FCSTD DOCUMENT  (FreeCAD 0.18.4R)
Label: 3-bedr_1fl_130720
License: All rights reserved
LicenseURL: http://en.wikipedia.org/wiki/All_rights_reserved
objects: Part::Part2DObjectPython×132, Part::Feature×3, Sketcher::SketchObject×2, Part::FeaturePython×2, App::DocumentObjectGroup×2
note: 139 computed .brp shape members not serialized (recipe doc carries the construction recipe); baked Part::Feature solids carry a one-line shape summary decoded from their .brp

FEATURE [Part::Part2DObjectPython] Rectangle1621  label="кровать_2сп_001"  # Draft 2D object (typed FeaturePython)
  ChamferSize = 0
  Columns = 1
  FilletRadius = 0
  Height = 1600
  Length = 2100
  MakeFace = false
  Placement = pos=(1550,11900,0) rot=(0,0,1;1.5708rad)
  Rows = 1
FEATURE [Part::Part2DObjectPython] Rectangle1622  label="тумба_001"  # Draft 2D object (typed FeaturePython)
  ChamferSize = 0
  Columns = 1
  FilletRadius = 0
  Height = 400
  Length = 400
  MakeFace = false
  Placement = pos=(-150,13600,0) rot=(0,0,1;1.5708rad)
  Rows = 1
FEATURE [Part::Part2DObjectPython] Rectangle1623  label="тумба_010"  # Draft 2D object (typed FeaturePython)
  ChamferSize = 0
  Columns = 1
  FilletRadius = 0
  Height = 400
  Length = 400
  MakeFace = false
  Placement = pos=(2050,13600,0) rot=(0,0,1;1.5708rad)
  Rows = 1
FEATURE [Part::Part2DObjectPython] Rectangle1624  # Draft 2D object (typed FeaturePython)
  ChamferSize = 0
  Columns = 1
  FilletRadius = 0
  Height = 600
  Length = 600
  MakeFace = false
  Placement = pos=(2950,13400,0) rot=(0,0,1;1.5708rad)
  Rows = 1
FEATURE [Part::Part2DObjectPython] Rectangle1625  # Draft 2D object (typed FeaturePython)
  ChamferSize = 0
  Columns = 1
  FilletRadius = 0
  Height = 600
  Length = 600
  MakeFace = false
  Placement = pos=(2950,12800,0) rot=(0,0,1;1.5708rad)
  Rows = 1
FEATURE [Part::Part2DObjectPython] Rectangle1626  # Draft 2D object (typed FeaturePython)
  ChamferSize = 0
  Columns = 1
  FilletRadius = 0
  Height = 600
  Length = 600
  MakeFace = false
  Placement = pos=(2950,12200,0) rot=(0,0,1;1.5708rad)
  Rows = 1
FEATURE [Part::Part2DObjectPython] Rectangle1628  # Draft 2D object (typed FeaturePython)
  ChamferSize = 0
  Columns = 1
  FilletRadius = 0
  Height = 3100
  Length = 3900
  MakeFace = false
  Placement = pos=(3200,10900,0) rot=(0,0,1;0rad)
  Rows = 1
FEATURE [Part::Part2DObjectPython] Wire351  # Draft 2D object (typed FeaturePython)
  ChamferSize = 0
  Closed = false
  End = (2950,12200,0)
  FilletRadius = 0
  Length = 5691.17
  MakeFace = false
  Placement = pos=(2350,12200,0) rot=(0,0,1;1.5708rad)
  Points = (8) [(0,0,0),(600,-600,0),(1200,0,0),(1800,-600,0),(1800,0,0),(1200,-600,0),(600,0,0),(0,-600,0)]
  Start = (2350,12200,0)
  Subdivisions = 0
FEATURE [Part::Part2DObjectPython] Rectangle1629  # Draft 2D object (typed FeaturePython)
  ChamferSize = 0
  Columns = 1
  FilletRadius = 0
  Height = 600
  Length = 600
  MakeFace = false
  Placement = pos=(3800,12200,0) rot=(0,0,1;1.5708rad)
  Rows = 1
FEATURE [Part::Part2DObjectPython] Rectangle1630  # Draft 2D object (typed FeaturePython)
  ChamferSize = 0
  Columns = 1
  FilletRadius = 0
  Height = 600
  Length = 600
  MakeFace = false
  Placement = pos=(3800,12800,0) rot=(0,0,1;1.5708rad)
  Rows = 1
FEATURE [Part::Part2DObjectPython] Rectangle1631  # Draft 2D object (typed FeaturePython)
  ChamferSize = 0
  Columns = 1
  FilletRadius = 0
  Height = 600
  Length = 600
  MakeFace = false
  Placement = pos=(3800,13400,0) rot=(0,0,1;1.5708rad)
  Rows = 1
FEATURE [Part::Part2DObjectPython] Wire352  # Draft 2D object (typed FeaturePython)
  ChamferSize = 0
  Closed = false
  End = (3800,12200,0)
  FilletRadius = 0
  Length = 5691.17
  MakeFace = false
  Placement = pos=(3200,12200,0) rot=(0,0,1;1.5708rad)
  Points = (8) [(0,0,0),(600,-600,0),(1200,0,0),(1800,-600,0),(1800,0,0),(1200,-600,0),(600,0,0),(0,-600,0)]
  Start = (3200,12200,0)
  Subdivisions = 0
FEATURE [Part::Part2DObjectPython] Rectangle1632  label="тумба_011"  # Draft 2D object (typed FeaturePython)
  ChamferSize = 0
  Columns = 1
  FilletRadius = 0
  Height = 400
  Length = 400
  MakeFace = false
  Placement = pos=(4500,13600,0) rot=(0,0,1;1.5708rad)
  Rows = 1
FEATURE [Part::Part2DObjectPython] Rectangle1633  label="кровать_2сп_002"  # Draft 2D object (typed FeaturePython)
  ChamferSize = 0
  Columns = 1
  FilletRadius = 0
  Height = 1600
  Length = 2100
  MakeFace = false
  Placement = pos=(6200,11900,0) rot=(0,0,1;1.5708rad)
  Rows = 1
FEATURE [Part::Part2DObjectPython] Rectangle1634  label="тумба_012"  # Draft 2D object (typed FeaturePython)
  ChamferSize = 0
  Columns = 1
  FilletRadius = 0
  Height = 400
  Length = 400
  MakeFace = false
  Placement = pos=(6700,13600,0) rot=(0,0,1;1.5708rad)
  Rows = 1
FEATURE [Part::Part2DObjectPython] Rectangle1635  label="Д-90_013"  # Draft 2D object (typed FeaturePython)
  ChamferSize = 0
  Columns = 1
  FilletRadius = 0
  Height = 900
  Length = 100
  MakeFace = true
  Placement = pos=(4250,10800,0) rot=(0,0,1;1.5708rad)
  Rows = 1
FEATURE [Part::Part2DObjectPython] Rectangle1636  label="Д-90_012"  # Draft 2D object (typed FeaturePython)
  ChamferSize = 0
  Columns = 1
  FilletRadius = 0
  Height = 900
  Length = 100
  MakeFace = true
  Placement = pos=(2800,10800,0) rot=(0,0,1;1.5708rad)
  Rows = 1
FEATURE [Part::Part2DObjectPython] Rectangle1639  # Draft 2D object (typed FeaturePython)
  ChamferSize = 0
  Columns = 1
  FilletRadius = 0
  Height = 1800
  Length = 2600
  MakeFace = false
  Placement = pos=(-900,9000,0) rot=(0,0,1;0rad)
  Rows = 1
FEATURE [Part::Part2DObjectPython] Rectangle1640  # Draft 2D object (typed FeaturePython)
  ChamferSize = 0
  Columns = 1
  FilletRadius = 0
  Height = 600
  Length = 600
  MakeFace = false
  Placement = pos=(1800,8300,0) rot=(0,0,1;1.5708rad)
  Rows = 1
FEATURE [Part::Part2DObjectPython] Rectangle1641  # Draft 2D object (typed FeaturePython)
  ChamferSize = 0
  Columns = 1
  FilletRadius = 0
  Height = 600
  Length = 600
  MakeFace = false
  Placement = pos=(1200,8300,0) rot=(0,0,1;1.5708rad)
  Rows = 1
FEATURE [Part::Part2DObjectPython] Rectangle1643  # Draft 2D object (typed FeaturePython)
  ChamferSize = 0
  Columns = 1
  FilletRadius = 0
  Height = 600
  Length = 600
  MakeFace = false
  Placement = pos=(300,8300,0) rot=(0,0,1;1.5708rad)
  Rows = 1
FEATURE [Part::Part2DObjectPython] Rectangle1644  # Draft 2D object (typed FeaturePython)
  ChamferSize = 0
  Columns = 1
  FilletRadius = 0
  Height = 600
  Length = 600
  MakeFace = false
  Placement = pos=(-300,8300,0) rot=(0,0,1;1.5708rad)
  Rows = 1
FEATURE [Part::Part2DObjectPython] Rectangle1645  # Draft 2D object (typed FeaturePython)
  ChamferSize = 0
  Columns = 1
  FilletRadius = 0
  Height = 1800
  Length = 1400
  MakeFace = false
  Placement = pos=(-900,7100,0) rot=(0,0,1;0rad)
  Rows = 1
FEATURE [Part::Part2DObjectPython] Rectangle1659  label="Д-90_009"  # Draft 2D object (typed FeaturePython)
  ChamferSize = 0
  Columns = 1
  FilletRadius = 0
  Height = 100
  Length = 900
  MakeFace = true
  Placement = pos=(600,7250,0) rot=(0,0,1;1.5708rad)
  Rows = 1
FEATURE [Part::Part2DObjectPython] Rectangle1660  label="Д-90_011"  # Draft 2D object (typed FeaturePython)
  ChamferSize = 0
  Columns = 1
  FilletRadius = 0
  Height = 100
  Length = 900
  MakeFace = true
  Placement = pos=(4500,9750,0) rot=(0,0,1;1.5708rad)
  Rows = 1
FEATURE [Part::Part2DObjectPython] Rectangle1663  label="Д-90_007"  # Draft 2D object (typed FeaturePython)
  ChamferSize = 0
  Columns = 1
  FilletRadius = 0
  Height = 400
  Length = 900
  MakeFace = true
  Placement = pos=(-900,7250,0) rot=(0,0,1;1.5708rad)
  Rows = 1
FEATURE [Part::Part2DObjectPython] Rectangle1665  # Draft 2D object (typed FeaturePython)
  ChamferSize = 0
  Columns = 1
  FilletRadius = 0
  Height = 3000
  Length = 2600
  MakeFace = false
  Placement = pos=(4500,7800,0) rot=(0,0,1;0rad)
  Rows = 1
FEATURE [Part::Part2DObjectPython] Rectangle1666  # Draft 2D object (typed FeaturePython)
  ChamferSize = 0
  Columns = 1
  FilletRadius = 0
  Height = 1800
  Length = 1200
  MakeFace = false
  Placement = pos=(3200,7700,0) rot=(0,0,1;0rad)
  Rows = 1
FEATURE [Part::Part2DObjectPython] Rectangle1668  # Draft 2D object (typed FeaturePython)
  ChamferSize = 0
  Columns = 1
  FilletRadius = 0
  Height = 600
  Length = 400
  MakeFace = false
  Placement = pos=(3600,8900,0) rot=(0,0,1;0rad)
  Rows = 1
FEATURE [Part::Part2DObjectPython] Circle042  # Draft 2D object (typed FeaturePython)
  FirstAngle = 0
  LastAngle = 0
  MakeFace = false
  Placement = pos=(3800,9100,0) rot=(0,0,1;0rad)
  Radius = 100
FEATURE [Part::Part2DObjectPython] Rectangle1671  label="Д-90_010"  # Draft 2D object (typed FeaturePython)
  ChamferSize = 0
  Columns = 1
  FilletRadius = 0
  Height = 100
  Length = 900
  MakeFace = true
  Placement = pos=(1800,9750,0) rot=(0,0,1;1.5708rad)
  Rows = 1
FEATURE [Part::Part2DObjectPython] Rectangle1672  # Draft 2D object (typed FeaturePython)
  ChamferSize = 0
  Columns = 1
  FilletRadius = 0
  Height = 400
  Length = 600
  MakeFace = false
  Placement = pos=(4400,7700,0) rot=(0,0,1;1.5708rad)
  Rows = 1
FEATURE [Part::Feature] Ellipse027
  Placement = pos=(4200,8000,0) rot=(0,0,1;1.5708rad)
  shape: bbox 200 x 400 x 2e-07 mm, 0 faces, 0 solids (baked)
FEATURE [Part::Part2DObjectPython] Rectangle1673  # Draft 2D object (typed FeaturePython)
  ChamferSize = 0
  Columns = 1
  FilletRadius = 0
  Height = 800
  Length = 1800
  MakeFace = false
  Placement = pos=(-100,9000,0) rot=(0,0,1;1.5708rad)
  Rows = 1
FEATURE [Part::Feature] Ellipse028
  Placement = pos=(-500,9900,0) rot=(0,0,1;1.5708rad)
  shape: bbox 600 x 1400 x 2e-07 mm, 0 faces, 0 solids (baked)
FEATURE [Part::Part2DObjectPython] Rectangle1674  # Draft 2D object (typed FeaturePython)
  ChamferSize = 0
  Columns = 1
  FilletRadius = 0
  Height = 400
  Length = 600
  MakeFace = false
  Placement = pos=(1400,9000,0) rot=(0,0,1;1.5708rad)
  Rows = 1
FEATURE [Part::Part2DObjectPython] Circle043  # Draft 2D object (typed FeaturePython)
  FirstAngle = 0
  LastAngle = 0
  MakeFace = false
  Placement = pos=(1200,9400,0) rot=(0,0,1;1.5708rad)
  Radius = 100
FEATURE [Part::Part2DObjectPython] Rectangle1675  # Draft 2D object (typed FeaturePython)
  ChamferSize = 0
  Columns = 1
  FilletRadius = 0
  Height = 600
  Length = 400
  MakeFace = false
  Placement = pos=(700,9000,0) rot=(0,0,1;1.5708rad)
  Rows = 1
FEATURE [Part::Feature] Ellipse029
  Placement = pos=(400,9200,0) rot=(0,0,1;3.14159rad)
  shape: bbox 400 x 200 x 2e-07 mm, 0 faces, 0 solids (baked)
FEATURE [Part::Part2DObjectPython] Rectangle1676  label="кровать_1.5сп_001"  # Draft 2D object (typed FeaturePython)
  ChamferSize = 0
  Columns = 1
  FilletRadius = 0
  Height = 1200
  Length = 2100
  MakeFace = false
  Placement = pos=(4500,7800,0) rot=(0,0,1;0rad)
  Rows = 1
FEATURE [Sketcher::SketchObject] Sketch214  label="стол угловой002"
  Placement = pos=(7100,10800,0) rot=(0,0,1;3.14159rad)
  sketch-geometry (9):
    g0: LineSegment StartX=1400 StartY=0 StartZ=0 EndX=0 EndY=0 EndZ=0
    g1: LineSegment StartX=0 StartY=0 StartZ=0 EndX=0 EndY=1300 EndZ=0
    g2: LineSegment StartX=0 StartY=1300 StartZ=0 EndX=370 EndY=1300 EndZ=0
    g3: LineSegment StartX=470 StartY=1200 StartZ=0 EndX=470 EndY=900 EndZ=0
    g4: LineSegment StartX=1400 StartY=0 StartZ=0 EndX=1400 EndY=500 EndZ=0
    g5: LineSegment StartX=1300 StartY=600 StartZ=0 EndX=770 EndY=600 EndZ=0
    g6: ArcOfCircle CenterX=770 CenterY=900 CenterZ=0 NormalX=0 NormalY=0 NormalZ=1 AngleXU=0 Radius=300 StartAngle=3.14159 EndAngle=4.71239
    g7: ArcOfCircle CenterX=1300 CenterY=500 CenterZ=0 NormalX=0 NormalY=0 NormalZ=1 AngleXU=0 Radius=100 StartAngle=1e-16 EndAngle=1.5708
    g8: ArcOfCircle CenterX=370 CenterY=1200 CenterZ=0 NormalX=0 NormalY=0 NormalZ=1 AngleXU=0 Radius=100 StartAngle=5e-16 EndAngle=1.5708
  constraints (25):
    c: Horizontal(g0)
    c: Coincident(g0,g1)
    c: Vertical(g1)
    c: Coincident(g1,g2)
    c: Horizontal(g2)
    c: Coincident(g0,g4)
    c: Horizontal(g5)
    c: Coincident(g6,g3)
    c: Coincident(g6,g5)
    c: Parallel(g3,g1)
    c: Distance(g1) = 1300
    c: Distance(g0) = 1400
    c: Vertical(g4)
    c: Coincident(g0,g-1)
    c: Radius(g6) = 300
    c: DistanceY(g5,g6) = 300
    c: DistanceY(g6,g3) = 0
    c: Tangent(g5,g7) = -1.5708
    c: Tangent(g4,g7) = -1.5708
    c: Radius(g7) = 100
    c: DistanceY(g0,g5) = 600
    c: Tangent(g2,g8) = 1.5708
    c: Tangent(g3,g8) = 1.5708
    c: Radius(g8) = 100
    c: DistanceX(g1,g3) = 470
FEATURE [Sketcher::SketchObject] Sketch215  label="кресло 45'002"
  Placement = pos=(6347.49,9947.49,0) rot=(0,0,1;2.35619rad)
  sketch-geometry (11):
    g0: LineSegment StartX=-280 StartY=-350 StartZ=0 EndX=280 EndY=-350 EndZ=0
    g1: LineSegment StartX=330 StartY=-300 StartZ=0 EndX=330 EndY=300 EndZ=0
    g2: LineSegment StartX=280 StartY=350 StartZ=0 EndX=-280 EndY=350 EndZ=0
    g3: LineSegment StartX=-330 StartY=300 StartZ=0 EndX=-330 EndY=-300 EndZ=0
    g4: ArcOfCircle CenterX=-280 CenterY=300 CenterZ=0 NormalX=0 NormalY=0 NormalZ=1 AngleXU=0 Radius=50 StartAngle=1.5708 EndAngle=3.14159
    g5: ArcOfCircle CenterX=280 CenterY=300 CenterZ=0 NormalX=0 NormalY=0 NormalZ=1 AngleXU=0 Radius=50 StartAngle=-9e-16 EndAngle=1.5708
    g6: ArcOfCircle CenterX=280 CenterY=-300 CenterZ=0 NormalX=0 NormalY=0 NormalZ=1 AngleXU=0 Radius=50 StartAngle=4.71239 EndAngle=6.28319
    g7: ArcOfCircle CenterX=-280 CenterY=-300 CenterZ=0 NormalX=0 NormalY=0 NormalZ=1 AngleXU=0 Radius=50 StartAngle=3.14159 EndAngle=4.71239
    g8: LineSegment StartX=-330 StartY=200 StartZ=0 EndX=330 EndY=200 EndZ=0
    g9: LineSegment StartX=-230 StartY=200 StartZ=0 EndX=-230 EndY=-350 EndZ=0
    g10: LineSegment StartX=230 StartY=200 StartZ=0 EndX=230 EndY=-350 EndZ=0
  constraints (29):
    c: Horizontal(g0)
    c: Vertical(g1)
    c: Vertical(g3)
    c: Tangent(g2,g4) = -1.5708
    c: Tangent(g3,g4) = -1.5708
    c: Tangent(g2,g5) = -1.5708
    c: Tangent(g1,g5) = -1.5708
    c: Tangent(g0,g6) = -1.5708
    c: Tangent(g1,g6) = -1.5708
    c: Tangent(g3,g7) = -1.5708
    c: Tangent(g0,g7) = -1.5708
    c: DistanceY(g0,g2) = 700
    c: DistanceX(g3,g1) = 660
    c: Equal(g4,g5)
    c: Equal(g7,g6)
    c: Radius(g5) = 50
    c: Symmetric(g2,g2,g-2)
    c: Symmetric(g2,g0,g-1)
    c: PointOnObject(g8,g3)
    c: PointOnObject(g8,g1)
    c: Horizontal(g8)
    c: DistanceY(g8,g2) = 150
    c: PointOnObject(g9,g8)
    c: PointOnObject(g9,g0)
    c: Vertical(g9)
    c: PointOnObject(g10,g0)
    c: Vertical(g10)
    c: DistanceX(g10,g8) = 100
    c: Symmetric(g10,g9,g-2)
FEATURE [Part::Part2DObjectPython] Rectangle1677  label="шкаф_002"  # Draft 2D object (typed FeaturePython)
  ChamferSize = 0
  Columns = 1
  FilletRadius = 0
  Height = 1500
  Length = 450
  MakeFace = false
  Placement = pos=(6650,7800,0) rot=(0,0,1;0rad)
  Rows = 1
FEATURE [Part::Part2DObjectPython] Rectangle1680  # Draft 2D object (typed FeaturePython)
  ChamferSize = 0
  Columns = 1
  FilletRadius = 0
  Height = 1000
  Length = 3850
  MakeFace = false
  Placement = pos=(-900,6000,0) rot=(0,0,1;0rad)
  Rows = 1
FEATURE [Part::Part2DObjectPython] Rectangle1683  # Draft 2D object (typed FeaturePython)
  ChamferSize = 0
  Columns = 1
  FilletRadius = 0
  Height = 3275
  Length = 250
  MakeFace = false
  Placement = pos=(2950,3525,0) rot=(0,0,1;0rad)
  Rows = 1
FEATURE [Part::Part2DObjectPython] Wire356  # Draft 2D object (typed FeaturePython)
  ChamferSize = 0
  Closed = true
  End = (1800,8900,0)
  FilletRadius = 0
  Length = 4594.11
  MakeFace = false
  Placement = pos=(1800,8300,0) rot=(0,0,1;1.5708rad)
  Points = (6) [(0,600,0),(600,1200,0),(0,1200,0),(600,600,0),(0,-2.27374e-13,0),(600,0,0)]
  Start = (1200,8300,0)
  Subdivisions = 0
FEATURE [Part::Part2DObjectPython] Circle044  # Draft 2D object (typed FeaturePython)
  FirstAngle = 0
  LastAngle = 0
  MakeFace = false
  Placement = pos=(-10100,-3800,0) rot=(0,0,1;1.5708rad)
  Radius = 75
FEATURE [Part::FeaturePython] Array001  # Draft array (typed FeaturePython)
  Angle = 360
  ArrayType = 0
  Axis = (0,0,1)
  Base = -> Circle044
  Center = (0,0,0)
  Fuse = false
  IntervalAxis = (0,0,0)
  IntervalX = (250,0,0)
  IntervalY = (0,250,0)
  IntervalZ = (0,0,1)
  NumberPolar = 1
  NumberX = 2
  NumberY = 2
  NumberZ = 1
  Placement = pos=(11200,-500,0) rot=(0,0,1;1.5708rad)
FEATURE [Part::Part2DObjectPython] ShapeString051  label="надпись 052"  # Draft 2D object (typed FeaturePython)
  FontFile = <path>
  Placement = pos=(4718.84,6023.87,0) rot=(0,0,1;0rad)
  Size = 200
  String = Х
  Tracking = 0
FEATURE [Part::Part2DObjectPython] ShapeString052  label="надпись 053"  # Draft 2D object (typed FeaturePython)
  FontFile = <path>
  Placement = pos=(5211.98,3398.06,0) rot=(0,0,1;0rad)
  Size = 200
  String = ПМ
  Tracking = 0
FEATURE [Part::Part2DObjectPython] Rectangle1685  # Draft 2D object (typed FeaturePython)
  ChamferSize = 0
  Columns = 1
  FilletRadius = 0
  Height = 600
  Length = 600
  MakeFace = false
  Placement = pos=(7100,7100,0) rot=(0,0,1;1.5708rad)
  Rows = 1
FEATURE [Part::Part2DObjectPython] ShapeString053  label="надпись 054"  # Draft 2D object (typed FeaturePython)
  FontFile = <path>
  Placement = pos=(5959.55,7315.43,0) rot=(0,0,1;0rad)
  Size = 200
  String = СшМ
  Tracking = 0
FEATURE [Part::Part2DObjectPython] Rectangle1686  # Draft 2D object (typed FeaturePython)
  ChamferSize = 0
  Columns = 1
  FilletRadius = 0
  Height = 600
  Length = 600
  MakeFace = false
  Placement = pos=(6500,7100,0) rot=(0,0,1;1.5708rad)
  Rows = 1
FEATURE [Part::Part2DObjectPython] ShapeString054  label="надпись 055"  # Draft 2D object (typed FeaturePython)
  FontFile = <path>
  Placement = pos=(6622.1,7310.04,0) rot=(0,0,1;0rad)
  Size = 200
  String = СМ
  Tracking = 0
FEATURE [Part::Part2DObjectPython] Rectangle1687  # Draft 2D object (typed FeaturePython)
  ChamferSize = 0
  Columns = 1
  FilletRadius = 0
  Height = 400
  Length = 500
  MakeFace = false
  Placement = pos=(4950.18,7090.81,0) rot=(0,0,1;1.5708rad)
  Rows = 1
FEATURE [Part::Part2DObjectPython] ShapeString055  label="надпись 056"  # Draft 2D object (typed FeaturePython)
  FontFile = <path>
  Placement = pos=(4580.51,7258.99,0) rot=(0,0,1;0rad)
  Size = 200
  String = Кт
  Tracking = 0
FEATURE [Part::Part2DObjectPython] Rectangle1690  # Draft 2D object (typed FeaturePython)
  ChamferSize = 0
  Columns = 1
  FilletRadius = 0
  Height = 900
  Length = 900
  MakeFace = false
  Placement = pos=(900,3200,0) rot=(0,0,1;1.5708rad)
  Rows = 1
FEATURE [Part::Part2DObjectPython] Rectangle1692  # Draft 2D object (typed FeaturePython)
  ChamferSize = 0
  Columns = 1
  FilletRadius = 0
  Height = 1500
  Length = 100
  MakeFace = false
  Placement = pos=(1150,6800,0) rot=(0,0,1;1.5708rad)
  Rows = 1
FEATURE [Part::Part2DObjectPython] Rectangle1693  # Draft 2D object (typed FeaturePython)
  ChamferSize = 0
  Columns = 1
  FilletRadius = 0
  Height = 900
  Length = 900
  MakeFace = false
  Placement = pos=(1800,3200,0) rot=(0,0,1;1.5708rad)
  Rows = 1
FEATURE [Part::Part2DObjectPython] Rectangle1699  # Draft 2D object (typed FeaturePython)
  ChamferSize = 0
  Columns = 1
  FilletRadius = 0
  Height = 300
  Length = 450
  MakeFace = false
  Placement = pos=(3700,4600,0) rot=(0,0,1;1.5708rad)
  Rows = 1
FEATURE [Part::Part2DObjectPython] Rectangle1700  # Draft 2D object (typed FeaturePython)
  ChamferSize = 0
  Columns = 1
  FilletRadius = 0
  Height = 300
  Length = 450
  MakeFace = false
  Placement = pos=(3700,5200,0) rot=(0,0,1;1.5708rad)
  Rows = 1
FEATURE [Part::Part2DObjectPython] Rectangle1701  # Draft 2D object (typed FeaturePython)
  ChamferSize = 0
  Columns = 1
  FilletRadius = 0
  Height = 750
  Length = 1400
  MakeFace = false
  Placement = pos=(3400,4400,0) rot=(0,0,1;1.5708rad)
  Rows = 1
FEATURE [Part::Part2DObjectPython] Rectangle1702  # Draft 2D object (typed FeaturePython)
  ChamferSize = 0
  Columns = 1
  FilletRadius = 0
  Height = 900
  Length = 900
  MakeFace = false
  Placement = pos=(9.095e-13,3200,0) rot=(0,0,1;1.5708rad)
  Rows = 1
FEATURE [Part::Part2DObjectPython] Rectangle1705  # Draft 2D object (typed FeaturePython)
  ChamferSize = 0
  Columns = 1
  FilletRadius = 0
  Height = 11600
  Length = 8800
  MakeFace = false
  Placement = pos=(-1300,2800,0) rot=(0,0,1;0rad)
  Rows = 1
FEATURE [Part::Part2DObjectPython] Rectangle1706  # Draft 2D object (typed FeaturePython)
  ChamferSize = 0
  Columns = 1
  FilletRadius = 0
  Height = 750
  Length = 600
  MakeFace = false
  Placement = pos=(4500,5700,0) rot=(0,0,1;0rad)
  Rows = 1
FEATURE [Part::Part2DObjectPython] ShapeString056  label="надпись 057"  # Draft 2D object (typed FeaturePython)
  FontFile = <path>
  Placement = pos=(4707.38,3404.17,0) rot=(0,0,1;0rad)
  Size = 200
  String = Х
  Tracking = 0
FEATURE [Part::Part2DObjectPython] ShapeString057  label="надпись 058"  # Draft 2D object (typed FeaturePython)
  FontFile = <path>
  Placement = pos=(-678.733,7585.68,0) rot=(0,0,1;0rad)
  Size = 200
  String = 2.5 м2
  Tracking = 0
FEATURE [Part::Part2DObjectPython] ShapeString058  label="надпись 059"  # Draft 2D object (typed FeaturePython)
  FontFile = <path>
  Placement = pos=(94.7917,4343.06,0) rot=(0,0,1;0rad)
  Size = 200
  String = общая: 86.4 м2
  Tracking = 0
FEATURE [Part::Part2DObjectPython] ShapeString059  label="надпись 060"  # Draft 2D object (typed FeaturePython)
  FontFile = <path>
  Placement = pos=(5103.91,4383.33,0) rot=(0,0,1;0rad)
  Size = 200
  String = 6.5 м2
  Tracking = 0
FEATURE [Part::Part2DObjectPython] ShapeString060  label="надпись 061"  # Draft 2D object (typed FeaturePython)
  FontFile = <path>
  Placement = pos=(5045.75,9315.62,0) rot=(0,0,1;0rad)
  Size = 200
  String = 7,8 м2
  Tracking = 0
FEATURE [Part::Part2DObjectPython] ShapeString061  label="надпись 062"  # Draft 2D object (typed FeaturePython)
  FontFile = <path>
  Placement = pos=(3342.88,8524.74,0) rot=(0,0,1;0rad)
  Size = 200
  String = 2.2 м2
  Tracking = 0
FEATURE [Part::Part2DObjectPython] ShapeString062  label="надпись 063"  # Draft 2D object (typed FeaturePython)
  FontFile = <path>
  Placement = pos=(4725.26,11395.7,0) rot=(0,0,1;0rad)
  Size = 200
  String = 12 м2
  Tracking = 0
FEATURE [Part::Part2DObjectPython] ShapeString063  label="надпись 064"  # Draft 2D object (typed FeaturePython)
  FontFile = <path>
  Placement = pos=(1676.22,7683.33,0) rot=(0,0,1;0rad)
  Size = 200
  String = 8.5 м2
  Tracking = 0
FEATURE [Part::Part2DObjectPython] ShapeString064  label="надпись 065"  # Draft 2D object (typed FeaturePython)
  FontFile = <path>
  Placement = pos=(79.2535,9812.37,0) rot=(0,0,1;0rad)
  Size = 200
  String = 4,7 м2
  Tracking = 0
FEATURE [Part::Part2DObjectPython] ShapeString065  label="надпись 066"  # Draft 2D object (typed FeaturePython)
  FontFile = <path>
  Placement = pos=(228.385,11411.1,0) rot=(0,0,1;0rad)
  Size = 200
  String = 11,9 м2
  Tracking = 0
FEATURE [Part::Part2DObjectPython] ShapeString066  label="надпись 067"  # Draft 2D object (typed FeaturePython)
  FontFile = <path>
  Placement = pos=(5451.04,6700,0) rot=(0,0,1;0rad)
  Size = 200
  String = 5.2 м2
  Tracking = 0
FEATURE [Part::Part2DObjectPython] Rectangle1707  label="ОК-120_001"  # Draft 2D object (typed FeaturePython)
  ChamferSize = 0
  Columns = 1
  FilletRadius = 0
  Height = 400
  Length = 1200
  MakeFace = true
  Placement = pos=(-900,11600,0) rot=(0,0,1;1.5708rad)
  Rows = 1
FEATURE [Part::Part2DObjectPython] Rectangle1708  label="ОК-120_007"  # Draft 2D object (typed FeaturePython)
  ChamferSize = 0
  Columns = 1
  FilletRadius = 0
  Height = 400
  Length = 1200
  MakeFace = true
  Placement = pos=(7500,11600,0) rot=(0,0,1;1.5708rad)
  Rows = 1
FEATURE [Part::Part2DObjectPython] Rectangle1716  label="OK-90_001"  # Draft 2D object (typed FeaturePython)
  ChamferSize = 0
  Columns = 1
  FilletRadius = 0
  Height = 400
  Length = 900
  MakeFace = true
  Placement = pos=(-900,9400,0) rot=(0,0,1;1.5708rad)
  Rows = 1
FEATURE [Part::Part2DObjectPython] ShapeString067  label="надпись 068"  # Draft 2D object (typed FeaturePython)
  FontFile = <path>
  Placement = pos=(667.361,4991.49,0) rot=(0,0,1;0rad)
  Size = 200
  String = 19.5 м2
  Tracking = 0
FEATURE [Part::Part2DObjectPython] Rectangle1717  # Draft 2D object (typed FeaturePython)
  ChamferSize = 0
  Columns = 1
  FilletRadius = 0
  Height = 9800
  Length = 15000
  MakeFace = false
  Placement = pos=(8000,-100,0) rot=(0,0,1;1.5708rad)
  Rows = 1
FEATURE [Part::Part2DObjectPython] Line1006  # Draft 2D object (typed FeaturePython)
  ChamferSize = 0
  Closed = false
  End = (3100,14900,0)
  FilletRadius = 0
  Length = 15000
  MakeFace = false
  Placement = pos=(-3800,-7900,0) rot=(0,0,1;1.5708rad)
  Points = (2) [(7800,-6900,0),(22800,-6900,0)]
  Start = (3100,-100,0)
  Subdivisions = 0
FEATURE [Part::Part2DObjectPython] Rectangle  # Draft 2D object (typed FeaturePython)
  ChamferSize = 0
  Columns = 1
  FilletRadius = 0
  Height = 3100
  Length = 3850
  MakeFace = false
  Placement = pos=(-900,10900,0) rot=(0,0,1;0rad)
  Rows = 1
FEATURE [Part::Part2DObjectPython] Wire  # Draft 2D object (typed FeaturePython)
  ChamferSize = 0
  Closed = false
  End = (-900,8300,0)
  FilletRadius = 0
  Length = 3994.11
  MakeFace = true
  Placement = pos=(-900,8900,0) rot=(0,0,1;0rad)
  Points = (6) [(0,0,0),(600,-600,0),(1200,-1.81899e-12,0),(1200,-600,0),(600,-1.81899e-12,0),(-1.13687e-13,-600,0)]
  Start = (-900,8900,0)
  Subdivisions = 0
FEATURE [Part::Part2DObjectPython] Rectangle1719  # Draft 2D object (typed FeaturePython)
  ChamferSize = 0
  Columns = 1
  FilletRadius = 0
  Height = 2000
  Length = 2600
  MakeFace = false
  Placement = pos=(4500,5700,0) rot=(0,0,1;0rad)
  Rows = 1
FEATURE [Part::Part2DObjectPython] Wire358  # Draft 2D object (typed FeaturePython)
  ChamferSize = 0
  Closed = true
  End = (1800,8900,0)
  FilletRadius = 0
  Length = 38150
  MakeFace = false
  Placement = pos=(1800,10800,0) rot=(0,0,1;0rad)
  Points = (23) [(0,0,0),(2600,0,0),(2600,-1200,0),(1150,-1200,0),(1150,-4000,0),(1150,-4000,0),(2600,-4000,0),(2600,-5200,0),(5300,-5200,0),(5300,-7600,0),+13 more]
  Start = (1800,10800,0)
  Subdivisions = 0
FEATURE [Part::Part2DObjectPython] Rectangle1725  label="OK-90_007"  # Draft 2D object (typed FeaturePython)
  ChamferSize = 0
  Columns = 1
  FilletRadius = 0
  Height = 400
  Length = 900
  MakeFace = true
  Placement = pos=(7500,9400,0) rot=(0,0,1;1.5708rad)
  Rows = 1
FEATURE [Part::Part2DObjectPython] Rectangle1726  label="Д-90_001"  # Draft 2D object (typed FeaturePython)
  ChamferSize = 0
  Columns = 1
  FilletRadius = 0
  Height = 400
  Length = 900
  MakeFace = true
  Placement = pos=(7500,6100,0) rot=(0,0,1;1.5708rad)
  Rows = 1
FEATURE [Part::Part2DObjectPython] Rectangle1727  # Draft 2D object (typed FeaturePython)
  ChamferSize = 0
  Columns = 1
  FilletRadius = 0
  Height = 600
  Length = 300
  MakeFace = false
  Placement = pos=(7100,5300,0) rot=(0,0,1;1.5708rad)
  Rows = 1
FEATURE [Part::Part2DObjectPython] Rectangle1728  # Draft 2D object (typed FeaturePython)
  ChamferSize = 0
  Columns = 1
  FilletRadius = 0
  Height = 600
  Length = 600
  MakeFace = false
  Placement = pos=(7100,4700,0) rot=(0,0,1;1.5708rad)
  Rows = 1
FEATURE [Part::Part2DObjectPython] Rectangle1729  # Draft 2D object (typed FeaturePython)
  ChamferSize = 0
  Columns = 1
  FilletRadius = 0
  Height = 600
  Length = 900
  MakeFace = false
  Placement = pos=(7100,3800,0) rot=(0,0,1;1.5708rad)
  Rows = 1
FEATURE [Part::Part2DObjectPython] Rectangle1732  label="Д-90_008"  # Draft 2D object (typed FeaturePython)
  ChamferSize = 0
  Columns = 1
  FilletRadius = 0
  Height = 400
  Length = 900
  MakeFace = true
  Placement = pos=(3375,2800,0) rot=(0,0,1;0rad)
  Rows = 1
FEATURE [Part::Part2DObjectPython] Rectangle1733  label="OK-90_008"  # Draft 2D object (typed FeaturePython)
  ChamferSize = 0
  Columns = 1
  FilletRadius = 0
  Height = 400
  Length = 900
  MakeFace = true
  Placement = pos=(1850,2800,0) rot=(0,0,1;0rad)
  Rows = 1
FEATURE [Part::Part2DObjectPython] Rectangle1734  label="Д-70_001"  # Draft 2D object (typed FeaturePython)
  ChamferSize = 0
  Columns = 1
  FilletRadius = 0
  Height = 700
  Length = 100
  MakeFace = true
  Placement = pos=(5950,5600,0) rot=(0,0,1;1.5708rad)
  Rows = 1
FEATURE [Part::Part2DObjectPython] Rectangle1735  label="Д-70_002"  # Draft 2D object (typed FeaturePython)
  ChamferSize = 0
  Columns = 1
  FilletRadius = 0
  Height = 250
  Length = 700
  MakeFace = true
  Placement = pos=(3200,7800,0) rot=(0,0,1;1.5708rad)
  Rows = 1
FEATURE [Part::Part2DObjectPython] Rectangle1736  label="шкаф_001"  # Draft 2D object (typed FeaturePython)
  ChamferSize = 0
  Columns = 1
  FilletRadius = 0
  Height = 450
  Length = 2600
  MakeFace = false
  Placement = pos=(-900,6550,0) rot=(0,0,1;0rad)
  Rows = 1
FEATURE [Part::Part2DObjectPython] Rectangle1738  label="ОК-120_010"  # Draft 2D object (typed FeaturePython)
  ChamferSize = 0
  Columns = 1
  FilletRadius = 0
  Height = 400
  Length = 1200
  MakeFace = true
  Placement = pos=(5300,2800,0) rot=(0,0,1;0rad)
  Rows = 1
FEATURE [Part::Part2DObjectPython] Rectangle1739  label="ОК-120_009"  # Draft 2D object (typed FeaturePython)
  ChamferSize = 0
  Columns = 1
  FilletRadius = 0
  Height = 400
  Length = 1200
  MakeFace = true
  Placement = pos=(-300,2800,0) rot=(0,0,1;0rad)
  Rows = 1
FEATURE [Part::Part2DObjectPython] Rectangle1740  label="ОК-120_008"  # Draft 2D object (typed FeaturePython)
  ChamferSize = 0
  Columns = 1
  FilletRadius = 0
  Height = 400
  Length = 1200
  MakeFace = true
  Placement = pos=(-900,4400,0) rot=(0,0,1;1.5708rad)
  Rows = 1
FEATURE [Part::Part2DObjectPython] Rectangle1741  label="Rectangle1739"  # Draft 2D object (typed FeaturePython)
  ChamferSize = 0
  Columns = 1
  FilletRadius = 0
  Height = 600
  Length = 600
  MakeFace = false
  Placement = pos=(6500,3200,0) rot=(0,0,1;0rad)
  Rows = 1
FEATURE [Part::Part2DObjectPython] Rectangle1742  label="Rectangle1740"  # Draft 2D object (typed FeaturePython)
  ChamferSize = 0
  Columns = 1
  FilletRadius = 0
  Height = 900
  Length = 600
  MakeFace = false
  Placement = pos=(6500,3200,0) rot=(0,0,1;1.5708rad)
  Rows = 1
FEATURE [Part::Part2DObjectPython] Rectangle1743  label="Rectangle1741"  # Draft 2D object (typed FeaturePython)
  ChamferSize = 0
  Columns = 1
  FilletRadius = 0
  Height = 750
  Length = 600
  MakeFace = false
  Placement = pos=(5150,3200,0) rot=(0,0,1;1.5708rad)
  Rows = 1
FEATURE [Part::Part2DObjectPython] Wire359  # Draft 2D object (typed FeaturePython)
  ChamferSize = 0
  Closed = false
  End = (4850,5600,0)
  FilletRadius = 150
  Length = 2121.24
  MakeFace = true
  Placement = pos=(4400,5600,0) rot=(0,0,1;0rad)
  Points = (4) [(0,0,0),(9.09495e-13,-900,0),(450,-900,0),(450,0,0)]
  Start = (4400,5600,0)
  Subdivisions = 0
FEATURE [Part::Part2DObjectPython] Rectangle1744  label="Rectangle1742"  # Draft 2D object (typed FeaturePython)
  ChamferSize = 0
  Columns = 1
  FilletRadius = 0
  Height = 450
  Length = 600
  MakeFace = false
  Placement = pos=(5600,3200,0) rot=(0,0,1;1.5708rad)
  Rows = 1
FEATURE [Part::Part2DObjectPython] Rectangle1745  # Draft 2D object (typed FeaturePython)
  ChamferSize = 0
  Columns = 1
  FilletRadius = 50
  Height = 424.264
  Length = 500
  MakeFace = false
  Placement = pos=(5800,3300,0) rot=(0,0,1;0rad)
  Rows = 1
FEATURE [Part::Part2DObjectPython] Circle051  # Draft 2D object (typed FeaturePython)
  FirstAngle = 0
  LastAngle = 0
  MakeFace = false
  Placement = pos=(6700,4900,0) rot=(0,0,1;0rad)
  Radius = 75
FEATURE [Part::FeaturePython] Array002  # Draft array (typed FeaturePython)
  Angle = 360
  ArrayType = 0
  Axis = (0,0,1)
  Base = -> Circle051
  Center = (0,0,0)
  Fuse = false
  IntervalAxis = (0,0,0)
  IntervalX = (250,0,0)
  IntervalY = (0,250,0)
  IntervalZ = (0,0,1)
  NumberPolar = 1
  NumberX = 2
  NumberY = 2
  NumberZ = 1
FEATURE [Part::Part2DObjectPython] Rectangle1746  # Draft 2D object (typed FeaturePython)
  ChamferSize = 0
  Columns = 1
  FilletRadius = 0
  Height = 300
  Length = 450
  MakeFace = false
  Placement = pos=(2650,5200,0) rot=(0,0,1;1.5708rad)
  Rows = 1
FEATURE [Part::Part2DObjectPython] Rectangle1747  # Draft 2D object (typed FeaturePython)
  ChamferSize = 0
  Columns = 1
  FilletRadius = 0
  Height = 300
  Length = 450
  MakeFace = false
  Placement = pos=(2650,4600,0) rot=(0,0,1;1.5708rad)
  Rows = 1
FEATURE [Part::Part2DObjectPython] Line  # Draft 2D object (typed FeaturePython)
  ChamferSize = 0
  Closed = false
  End = (500,8300,0)
  FilletRadius = 0
  Length = 200
  MakeFace = true
  Placement = pos=(300,8300,0) rot=(0,0,1;0rad)
  Points = (2) [(0,0,0),(200,0,0)]
  Start = (300,8300,0)
  Subdivisions = 0
FEATURE [Part::Part2DObjectPython] Rectangle1748  # Draft 2D object (typed FeaturePython)
  ChamferSize = 0
  Columns = 1
  FilletRadius = 0
  Height = 2400
  Length = 8800
  MakeFace = false
  Placement = pos=(-1300,400,0) rot=(0,0,1;0rad)
  Rows = 1
FEATURE [Part::Part2DObjectPython] Arc  # Draft 2D object (typed FeaturePython)
  FirstAngle = -116.565
  LastAngle = 116.565
  MakeFace = true
  Placement = pos=(4950,5200,0) rot=(0,0,1;0rad)
  Radius = 223.607
FEATURE [Part::Part2DObjectPython] Circle  # Draft 2D object (typed FeaturePython)
  FirstAngle = 0
  LastAngle = 0
  MakeFace = false
  Placement = pos=(4800,6750,0) rot=(0,0,1;0rad)
  Radius = 250
FEATURE [Part::Part2DObjectPython] Rectangle1749  # Draft 2D object (typed FeaturePython)
  ChamferSize = 0
  Columns = 1
  FilletRadius = 0
  Height = 100
  Length = 800
  MakeFace = false
  Placement = pos=(5000,7600,0) rot=(0,0,1;0rad)
  Rows = 1
FEATURE [Part::Part2DObjectPython] Wire360  # Draft 2D object (typed FeaturePython)
  ChamferSize = 0
  Closed = false
  End = (7100,6050,0)
  FilletRadius = 100
  Length = 1407.08
  MakeFace = true
  Placement = pos=(6000,5700,0) rot=(0,0,1;0rad)
  Points = (3) [(0,0,0),(0,350,0),(1100,350,0)]
  Start = (6000,5700,0)
  Subdivisions = 0
FEATURE [Part::Part2DObjectPython] Rectangle1750  # Draft 2D object (typed FeaturePython)
  ChamferSize = 0
  Columns = 1
  FilletRadius = 0
  Height = 700
  Length = 1200
  MakeFace = true
  Placement = pos=(3200,6900,0) rot=(0,0,1;0rad)
  Rows = 1
FEATURE [Part::Part2DObjectPython] ShapeString068  label="надпись 069"  # Draft 2D object (typed FeaturePython)
  FontFile = <path>
  Placement = pos=(1803.91,1483.33,0) rot=(0,0,1;0rad)
  Size = 200
  String = 21.1 м2
  Tracking = 0
FEATURE [Part::Part2DObjectPython] Rectangle1751  # Draft 2D object (typed FeaturePython)
  ChamferSize = 0
  Columns = 1
  FilletRadius = 0
  Height = 1200
  Length = 250
  MakeFace = false
  Placement = pos=(2950,9600,0) rot=(0,0,1;0rad)
  Rows = 1
FEATURE [App::DocumentObjectGroup] Construction
FEATURE [Part::Part2DObjectPython] Arc002  # Draft 2D object (typed FeaturePython)
  FirstAngle = -90
  LastAngle = 0
  MakeFace = true
  Placement = pos=(5250,5600,0) rot=(0,0,1;0rad)
  Radius = 700
FEATURE [Part::Part2DObjectPython] Arc003  # Draft 2D object (typed FeaturePython)
  FirstAngle = -180
  LastAngle = -90
  MakeFace = true
  Placement = pos=(-1300,8150,0) rot=(0,0,1;0rad)
  Radius = 900
FEATURE [Part::Part2DObjectPython] Line1007  # Draft 2D object (typed FeaturePython)
  ChamferSize = 0
  Closed = false
  End = (-1300,8150,0)
  FilletRadius = 0
  Length = 900
  MakeFace = true
  Placement = pos=(-2200,8150,0) rot=(0,0,1;0rad)
  Points = (2) [(0,0,0),(900,0,0)]
  Start = (-2200,8150,0)
  Subdivisions = 0
FEATURE [Part::Part2DObjectPython] Arc004  # Draft 2D object (typed FeaturePython)
  FirstAngle = 180
  LastAngle = 270
  MakeFace = true
  Placement = pos=(4275,2800,0) rot=(0,0,1;0rad)
  Radius = 900
FEATURE [Part::Part2DObjectPython] Line1008  # Draft 2D object (typed FeaturePython)
  ChamferSize = 0
  Closed = false
  End = (4275,2800,0)
  FilletRadius = 0
  Length = 900
  MakeFace = true
  Placement = pos=(4275,1900,0) rot=(0,0,1;0rad)
  Points = (2) [(0,0,0),(0,900,0)]
  Start = (4275,1900,0)
  Subdivisions = 0
FEATURE [Part::Part2DObjectPython] Line1009  # Draft 2D object (typed FeaturePython)
  ChamferSize = 0
  Closed = false
  End = (5250,5600,0)
  FilletRadius = 0
  Length = 700
  MakeFace = true
  Placement = pos=(5250,4900,0) rot=(0,0,1;0rad)
  Points = (2) [(0,0,0),(0,700,0)]
  Start = (5250,4900,0)
  Subdivisions = 0
FEATURE [Part::Part2DObjectPython] Arc005  # Draft 2D object (typed FeaturePython)
  FirstAngle = -90
  LastAngle = 0
  MakeFace = true
  Placement = pos=(7500,7000,0) rot=(0,0,1;0rad)
  Radius = 900
FEATURE [Part::Part2DObjectPython] Line1010  # Draft 2D object (typed FeaturePython)
  ChamferSize = 0
  Closed = false
  End = (7500,7000,0)
  FilletRadius = 0
  Length = 900
  MakeFace = true
  Placement = pos=(8400,7000,0) rot=(0,0,1;0rad)
  Points = (2) [(0,0,0),(-900,9.09495e-13,0)]
  Start = (8400,7000,0)
  Subdivisions = 0
FEATURE [Part::Part2DObjectPython] Arc006  # Draft 2D object (typed FeaturePython)
  FirstAngle = -90
  LastAngle = 0
  MakeFace = true
  Placement = pos=(4500,10650,0) rot=(0,0,1;0rad)
  Radius = 900
FEATURE [Part::Part2DObjectPython] Line1011  # Draft 2D object (typed FeaturePython)
  ChamferSize = 0
  Closed = false
  End = (4500,10650,0)
  FilletRadius = 0
  Length = 900
  MakeFace = true
  Placement = pos=(5400,10650,0) rot=(0,0,1;0rad)
  Points = (2) [(0,0,0),(-900,0,0)]
  Start = (5400,10650,0)
  Subdivisions = 0
FEATURE [Part::Part2DObjectPython] Arc007  # Draft 2D object (typed FeaturePython)
  FirstAngle = 0
  LastAngle = 90
  MakeFace = true
  Placement = pos=(3350,10900,0) rot=(0,0,1;0rad)
  Radius = 900
FEATURE [Part::Part2DObjectPython] Line1012  # Draft 2D object (typed FeaturePython)
  ChamferSize = 0
  Closed = false
  End = (3350,10900,0)
  FilletRadius = 0
  Length = 900
  MakeFace = true
  Placement = pos=(3350,11800,0) rot=(0,0,1;0rad)
  Points = (2) [(0,0,0),(4.54747e-13,-900,0)]
  Start = (3350,11800,0)
  Subdivisions = 0
FEATURE [Part::Part2DObjectPython] Arc008  # Draft 2D object (typed FeaturePython)
  FirstAngle = 90
  LastAngle = 180
  MakeFace = true
  Placement = pos=(2800,10900,0) rot=(0,0,1;0rad)
  Radius = 900
FEATURE [Part::Part2DObjectPython] Line1013  # Draft 2D object (typed FeaturePython)
  ChamferSize = 0
  Closed = false
  End = (2800,10900,0)
  FilletRadius = 0
  Length = 900
  MakeFace = true
  Placement = pos=(2800,11800,0) rot=(0,0,1;0rad)
  Points = (2) [(0,0,0),(-9.09495e-13,-900,0)]
  Start = (2800,11800,0)
  Subdivisions = 0
FEATURE [Part::Part2DObjectPython] Arc009  # Draft 2D object (typed FeaturePython)
  FirstAngle = -180
  LastAngle = -90
  MakeFace = true
  Placement = pos=(1700,10650,0) rot=(0,0,1;0rad)
  Radius = 900
FEATURE [Part::Part2DObjectPython] Line1014  # Draft 2D object (typed FeaturePython)
  ChamferSize = 0
  Closed = false
  End = (1700,10650,0)
  FilletRadius = 0
  Length = 900
  MakeFace = true
  Placement = pos=(800,10650,0) rot=(0,0,1;0rad)
  Points = (2) [(0,0,0),(900,0,0)]
  Start = (800,10650,0)
  Subdivisions = 0
FEATURE [Part::Part2DObjectPython] Arc010  # Draft 2D object (typed FeaturePython)
  FirstAngle = 0
  LastAngle = 90
  MakeFace = true
  Placement = pos=(600,7250,0) rot=(0,0,1;0rad)
  Radius = 900
FEATURE [Part::Part2DObjectPython] Line1015  # Draft 2D object (typed FeaturePython)
  ChamferSize = 0
  Closed = false
  End = (1500,7250,0)
  FilletRadius = 0
  Length = 900
  MakeFace = true
  Placement = pos=(600,7250,0) rot=(0,0,1;0rad)
  Points = (2) [(0,0,0),(900,0,0)]
  Start = (600,7250,0)
  Subdivisions = 0
FEATURE [Part::Part2DObjectPython] Arc011  # Draft 2D object (typed FeaturePython)
  FirstAngle = -131.987
  LastAngle = -90
  MakeFace = true
  Placement = pos=(2950,8500,0) rot=(0,0,1;0rad)
  Radius = 700
FEATURE [Part::Part2DObjectPython] Line1016  # Draft 2D object (typed FeaturePython)
  ChamferSize = 0
  Closed = false
  End = (2950,8500,0)
  FilletRadius = 0
  Length = 700
  MakeFace = true
  Placement = pos=(2481.72,7979.69,0) rot=(0,0,1;0rad)
  Points = (2) [(0,0,0),(468.275,520.306,0)]
  Start = (2481.72,7979.69,0)
  Subdivisions = 0
FEATURE [Part::Part2DObjectPython] ShapeString069  label="надпись 070"  # Draft 2D object (typed FeaturePython)
  FontFile = <path>
  Placement = pos=(3448.78,7188.89,0) rot=(0,0,1;0rad)
  Size = 200
  String = ВЕНТ
  Tracking = 0
FEATURE [App::DocumentObjectGroup] Group  label="планировка 2сп+каб_87м2"
  Group = -> [Rectangle1621,Array001,Rectangle1622,Rectangle1623,Rectangle1624,Rectangle1625,Rectangle1626,Rectangle1628,Wire351,Rectangle1629,Rectangle1630,Rectangle1631,Wire352,Rectangle1632,Rectangle1633,Rectangle1634,Rectangle1635,Rectangle1636,Rectangle1639,Rectangle1640,Rectangle1641,Rectangle1643,Rectangle1644,Rectangle1645,Rectangle1659,Rectangle1660,Rectangle1663,Rectangle1665,Rectangle1666,+108 more]
note: 19 file-system paths scrubbed to <path> (originals preserved in the JSON sidecar)
